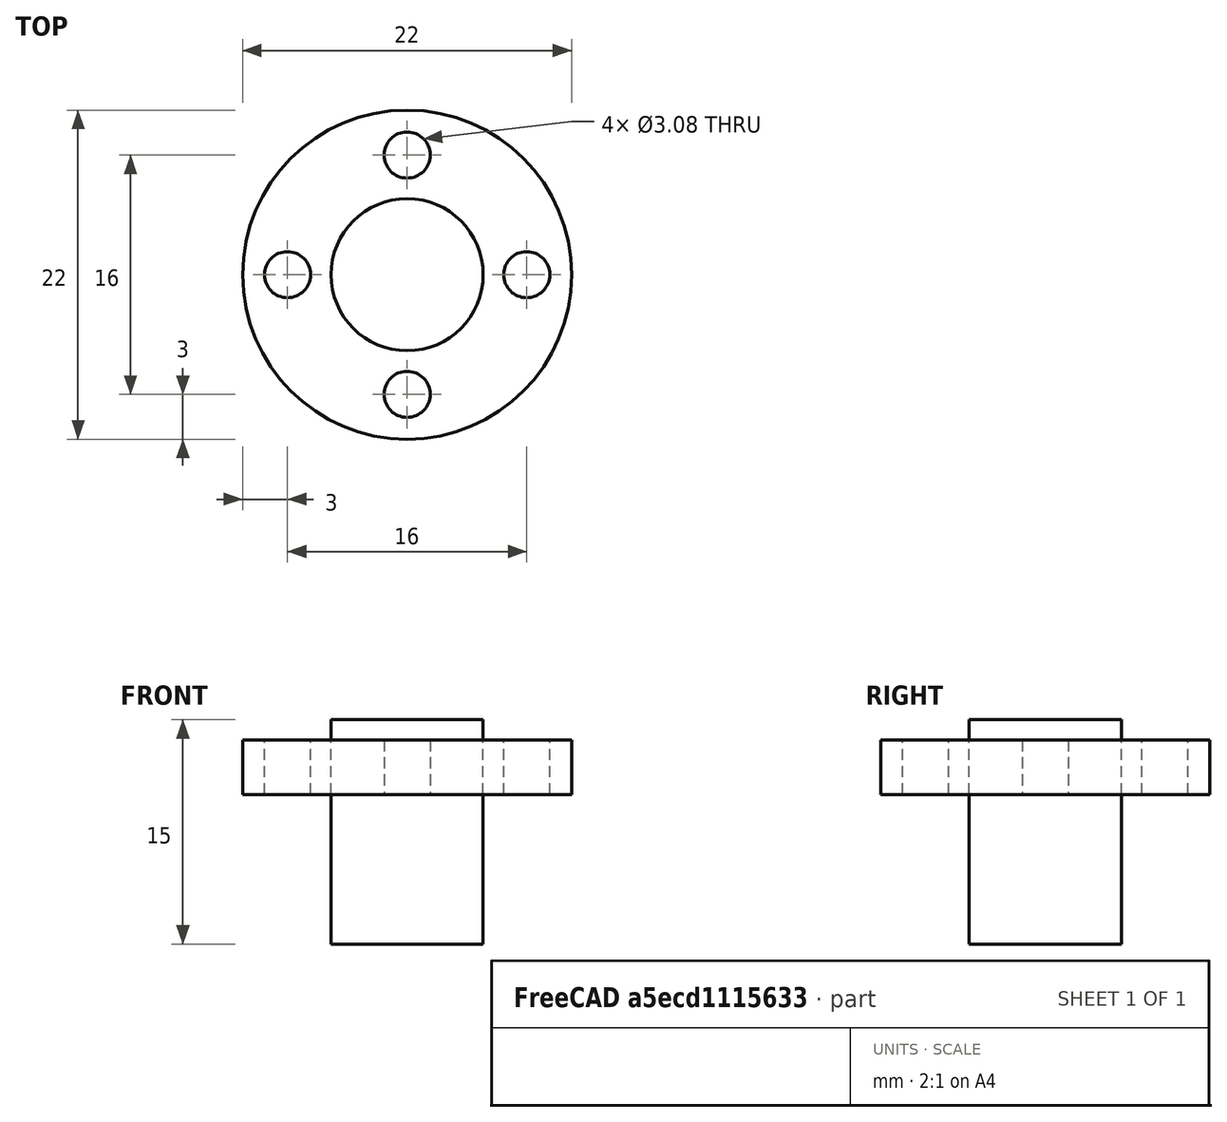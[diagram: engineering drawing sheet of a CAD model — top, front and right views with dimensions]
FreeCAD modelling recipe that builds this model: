
FCSTD DOCUMENT  (FreeCAD 0.14R3700 (Git))
Label: tuerca-husillo-z
License: CC-BY 3.0
LicenseURL: http://creativecommons.org/licenses/by/3.0/
objects: Part::Cylinder×2, Sketcher::SketchObject×1, PartDesign::Pocket×1, PartDesign::PolarPattern×1
note: 6 computed .brp shape members not serialized (recipe doc carries the construction recipe); baked Part::Feature solids carry a one-line shape summary decoded from their .brp

FEATURE [Part::Cylinder] Cylinder
  Angle = 360
  Height = 3.64
  Radius = 11
FEATURE [Part::Cylinder] Cylinder001
  Angle = 360
  Height = 15
  Placement = pos=(0,0,-10) rot=(0,0,1;0rad)
  Radius = 5.085
FEATURE [Sketcher::SketchObject] Sketch
  Placement = pos=(0,0,3.64) rot=(0,0,1;0rad)
  Support = -> Cylinder [Face2]
  sketch-geometry (1):
    g0: Circle CenterX=0 CenterY=-8 CenterZ=0 NormalX=0 NormalY=0 NormalZ=1 Radius=1.54127
  constraints (1):
    c: PointOnObject(g0,g-2)
FEATURE [PartDesign::Pocket] Pocket
  Length = 5
  Sketch = -> Sketch
  Type = 1
FEATURE [PartDesign::PolarPattern] PolarPattern
  Angle = 360
  Axis = -> Sketch [N_Axis]
  Occurrences = 4
  Originals = -> [Pocket]
